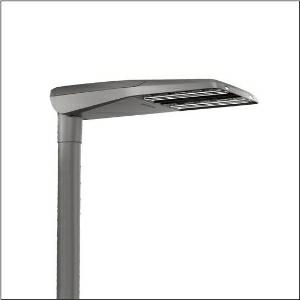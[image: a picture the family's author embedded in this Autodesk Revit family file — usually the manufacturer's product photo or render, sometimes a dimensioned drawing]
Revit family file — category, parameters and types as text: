
# Revit family: streetlight_sl_11_iq_midi___st0_5st0_5_5xc3h51e08me_bd44
name_source: partatom
category: Lighting Fixtures
units: mm (PartAtom-declared; Revit-internal decimal feet)

## family parameters
Cut with Voids When Loaded = No
Host = Face
Light Source = No
Part Type = Normal
Room Calculation Point = No
Round Connector Dimension = Use Diameter
Shared = No

## types (1)
- --- (1 x LED, 17940 lm, 124.7 W, 3000K)
    Apparent Load = 125 VA
    CIE Flux Codes = 43 74 97 100 100
    Color Rendering = 70
    Color Temperature = 3000K
    Default Elevation = 1800 mm
    Description = Streetlight SL 11 iQ midi, mast luminaire, primary light control with 3 zone facetted reflector, of plastic, silver coated, highly specular, primary optical cover: cover, of PMMA, transparent, light distribution: ST0.5ST0.5, light emission: direct distribution, primary light characteristic: asymmetric, installation type: post-top, side-entry, LED, High Power LED, rated luminous flux: 17.940lm, luminous efficacy: 144lm/W, light colour: 730, colour temperature: 3000K, control: optimised constant luminous flux control (CLO 2.0), Desk-Remote (wireless, voltage-free reading and setting of iQ features in the workshop via application-optimized NFC function/RFID function), Light-Fading, Smart-Wire, Night-Set, Lumen-Switch, Temp-Guard, Auto-Match, with cable H07RN-F 5x 1.5mm², mains connection: 220..240V, AC, 50/60Hz, connection cable pre-assembled, cable length: 12,5m, start of lifetime: 125W, end of lifetime: 132W, reduction: 61W, luminaire housing, of diecast aluminium, powder-coated, Siteco® metallic grey (DB 702S), length: 780mm, width: 376mm, height: 118mm, spigot size: 60/76mm (post-top) and 42/60/76mm (side-entry), mast flange for spigot size: 42mm: 5XC10008XM4, 60mm: 5XC10008XM2, 76/60mm: 5XC10108XM1, equipment: Power, protection rating (complete): IP66, insulation class (complete): insulation class II (safety insulation), certification: CE, ENEC, VDE, impact resistance: IK09, permissible operating ambient temperature for outdoor applications: -25..+50°C, standard-compliant lighting for roads and squares, packaging unit: 1 piece

Light Distribution: ST0.5ST0.5
    Height = 118 mm
    Lamp = 1 x LED
    Lamp Light Flux = 17940 lm
    Lamp Power = 124.7 W
    Lamp count = 1
    Length = 780 mm
    Luminous efficacy = 144 lm/W
    Manufacturer = Siteco
    ModVariant = No
    Model = 5XC3H51E08ME
    Number of Poles = 1
    OnlyDefault = Yes
    Power Factor = 1
    Product Name = Streetlight SL 11 iQ midi | ST0.5ST0.5
    Product group = mast luminaire | pylon top
    ProductGroupID = 6100
    Protection Class = Protection class II
    Protection Degree = IP 66
    RLX_Detail_Level = 1
    RlxData = <blob elided: 75217 chars, md5=5ab433e4>
    Socket = socket
    Standby Power = 0 W
    System Light Flux = 17941 lm
    System Power = 125 W
    Type Comments = factory setting: luminous flux: 100 % | dim-lin: 254 | 557 mA
    Type Image = l_1005960.jpg
    URL = http://relux.com
    VarID = @adj_086475
    Voltage = 0 V
    Weight = 0.00 kg
    Width = 376 mm

## geometry (parser evidence)
native form markers: Blend x4, Sweep x11
no freeform markers — native parametric forms only
